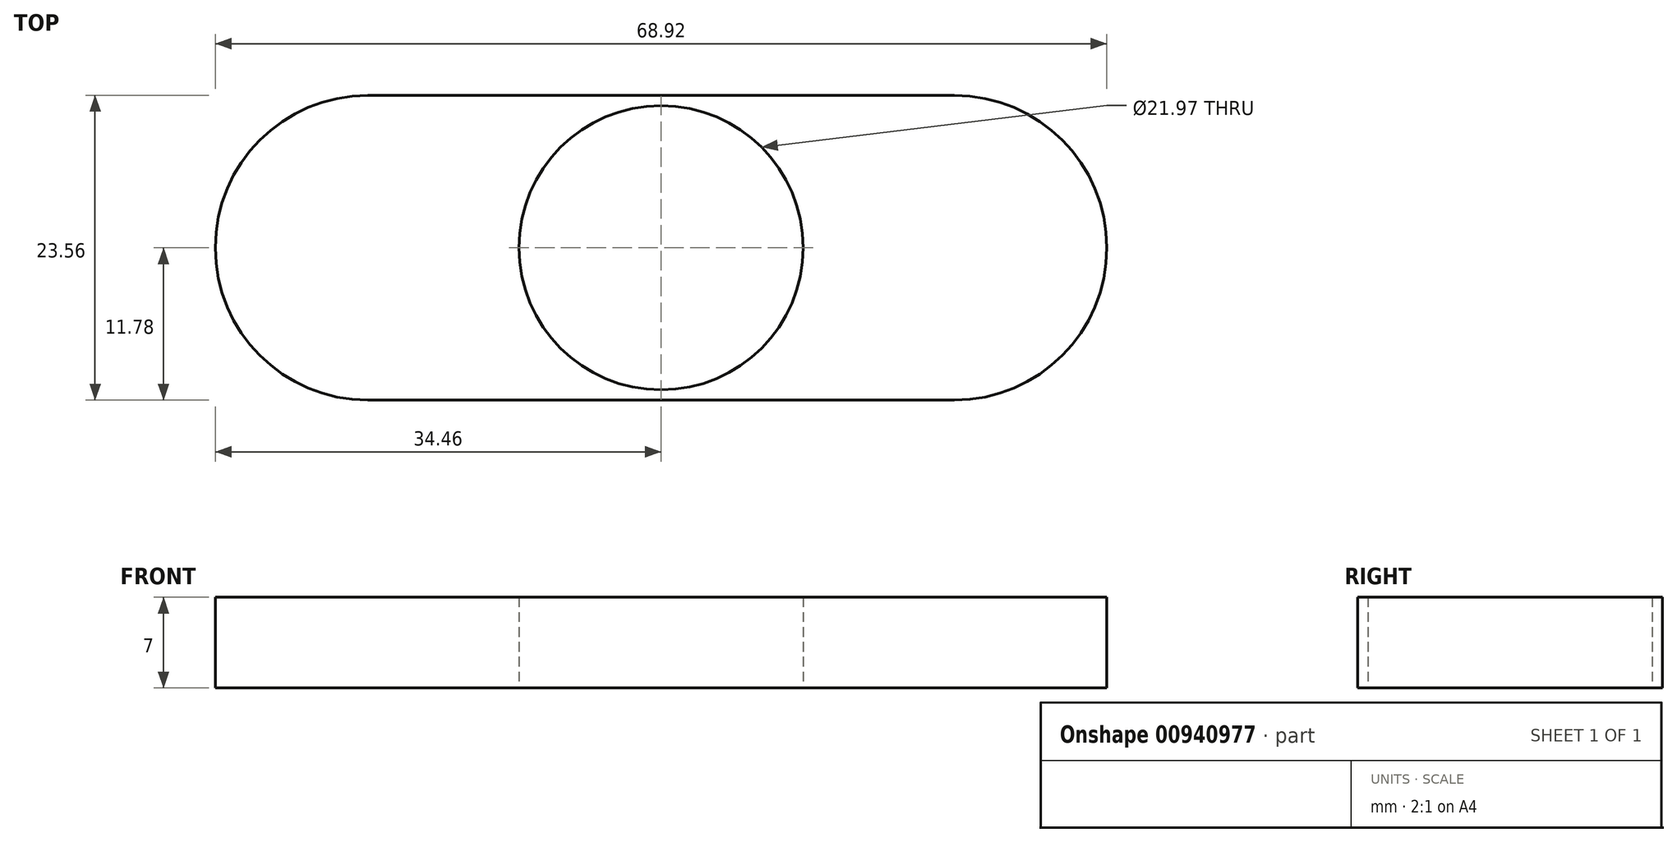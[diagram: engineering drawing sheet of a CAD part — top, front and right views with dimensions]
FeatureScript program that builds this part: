
annotation { "Feature Type Name" : "Feature", "Feature Type Description" : "" }
export const myFeature = defineFeature(function(context is Context, id is Id, definition is map)
    precondition{}
    {
        {
            var Q0;
            Q0=qCreatedBy(makeId("Top.planeOp"),FACE);
            var sketch = newSketch(context, id + "F0", { "sketchPlane" : qUnion([Q0])});
            skCircle(sketch, "E0", {"center": v(0, 0) * mm, "radius": 10.99 * mm});
            skLineSegment(sketch, "E1.bottom", {"start": v(-22.68, 11.78) * mm, "end": v(22.68, 11.78) * mm});
            skLineSegment(sketch, "E1.top", {"start": v(-22.68, -11.78) * mm, "end": v(22.68, -11.78) * mm});
            skLineSegment(sketch, "E1.left", {"start": v(-22.68, 11.78) * mm, "end": v(-22.68, -11.78) * mm});
            skLineSegment(sketch, "E1.right", {"start": v(22.68, 11.78) * mm, "end": v(22.68, -11.78) * mm});
            skCircle(sketch, "E2", {"center": v(-22.68, 0) * mm, "radius": 11.78 * mm});
            skCircle(sketch, "E3", {"center": v(22.68, 0) * mm, "radius": 11.78 * mm});
            skCircle(sketch, "E4", {"center": v(22.68, 0) * mm, "radius": 10.99 * mm});
            skCircle(sketch, "E5", {"center": v(-22.68, 0) * mm, "radius": 10.99 * mm});
            skSolve(sketch);
        }
        {
            var Q0;
            Q0 = qSketchRegion(id + "F0", true);
            var Q1;
            {var subQ0=sQuery(id+"F0.wireOp",EDGE,"E5");var subQ1=sQuery(id+"F0.wireOp",EDGE,"E1.left");var subQ2=makeQuery(id+"F0.imprint","INTERSECT",VERTEX,{"disambiguationData":[OD(0.0)],"derivedFrom":[subQ1,subQ0]});Q1=makeQuery(id+"F0.imprint","IMPRINT",FACE,{"disambiguationData":[TD([[makeQuery(id+"F0.imprint","IMPRINT",EDGE,{"disambiguationData":[TD([[subQ2,-1.0]])],"derivedFrom":subQ1}),-1.0]])]});}
            var Q2;
            {var subQ0=sQuery(id+"F0.wireOp",EDGE,"E5");var subQ1=sQuery(id+"F0.wireOp",EDGE,"E1.left");var subQ2=makeQuery(id+"F0.imprint","INTERSECT",VERTEX,{"disambiguationData":[OD(0.0)],"derivedFrom":[subQ1,subQ0]});Q2=makeQuery(id+"F0.imprint","IMPRINT",FACE,{"disambiguationData":[TD([[makeQuery(id+"F0.imprint","IMPRINT",EDGE,{"disambiguationData":[TD([[subQ2,-1.0]])],"derivedFrom":subQ1}),1.0]])]});}
            var Q3;
            {var subQ0=sQuery(id+"F0.wireOp",EDGE,"E4");var subQ1=sQuery(id+"F0.wireOp",EDGE,"E1.right");var subQ2=makeQuery(id+"F0.imprint","INTERSECT",VERTEX,{"disambiguationData":[OD(0.0)],"derivedFrom":[subQ1,subQ0]});Q3=makeQuery(id+"F0.imprint","IMPRINT",FACE,{"disambiguationData":[TD([[makeQuery(id+"F0.imprint","IMPRINT",EDGE,{"disambiguationData":[TD([[subQ2,-1.0]])],"derivedFrom":subQ1}),-1.0]])]});}
            var Q4;
            {var subQ0=sQuery(id+"F0.wireOp",EDGE,"E4");var subQ1=sQuery(id+"F0.wireOp",EDGE,"E1.right");var subQ2=makeQuery(id+"F0.imprint","INTERSECT",VERTEX,{"disambiguationData":[OD(0.0)],"derivedFrom":[subQ1,subQ0]});Q4=makeQuery(id+"F0.imprint","IMPRINT",FACE,{"disambiguationData":[TD([[makeQuery(id+"F0.imprint","IMPRINT",EDGE,{"disambiguationData":[TD([[subQ2,-1.0]])],"derivedFrom":subQ1}),1.0]])]});}
            extrude(context, id + "F1", {"entities" : qUnion([Q0, Q1, Q2, Q3, Q4]), "depth" : 7 * mm, "offsetDistance" : 25.4 * mm});
        }
    });
